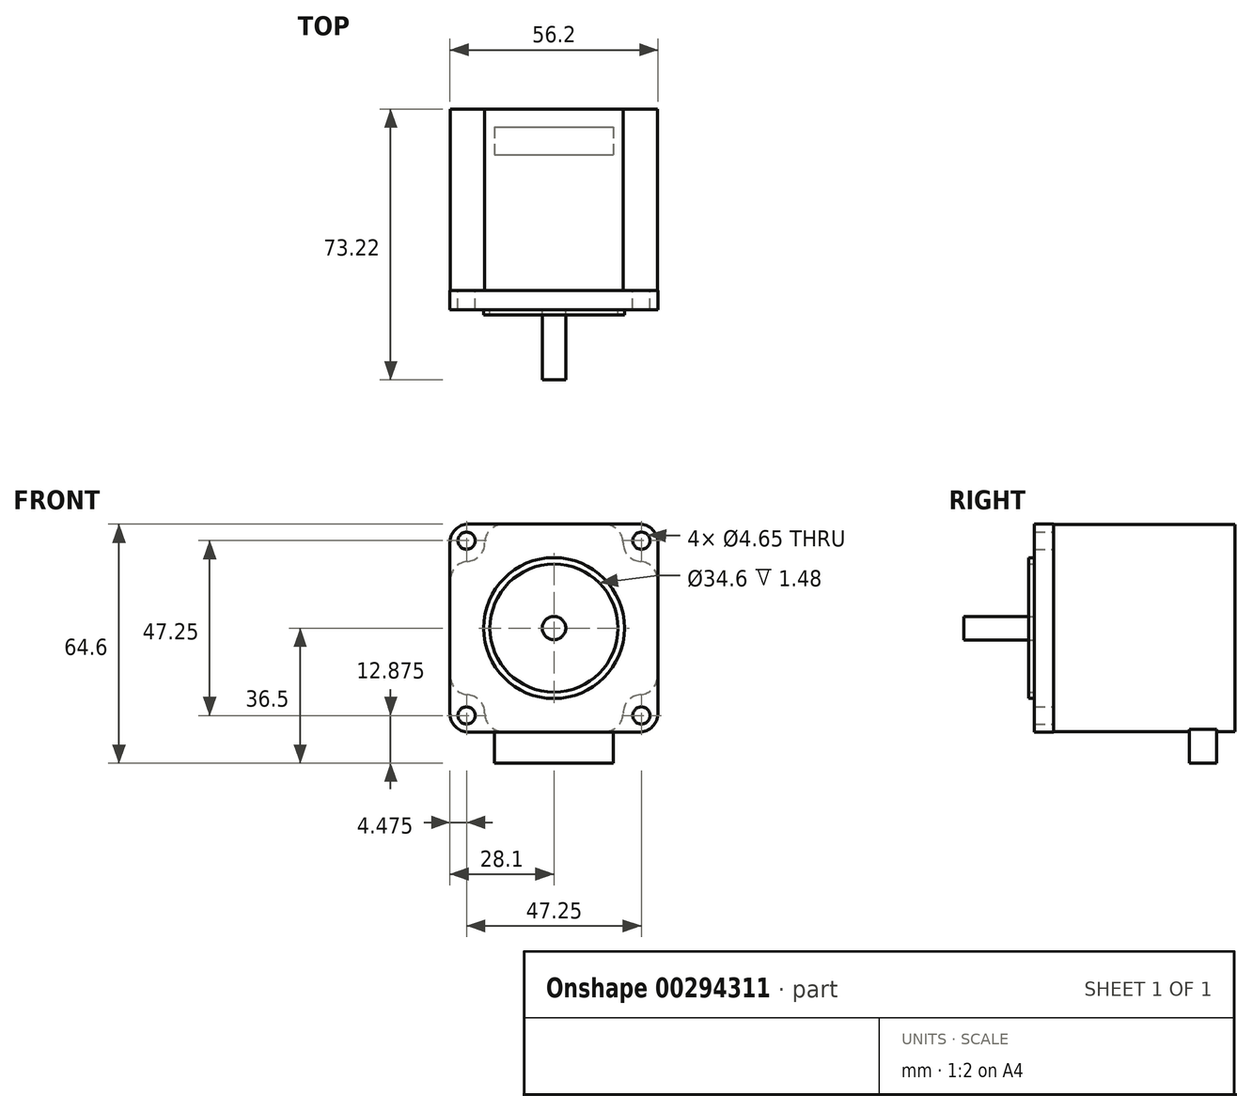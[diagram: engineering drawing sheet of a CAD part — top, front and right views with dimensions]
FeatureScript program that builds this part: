
annotation { "Feature Type Name" : "Feature", "Feature Type Description" : "" }
export const myFeature = defineFeature(function(context is Context, id is Id, definition is map)
    precondition{}
    {
        {
            var Q0;
            Q0=qCreatedBy(makeId("Front.planeOp"),FACE);
            var sketch = newSketch(context, id + "F0", { "sketchPlane" : qUnion([Q0])});
            skLineSegment(sketch, "E0.bottom", {"start": v(23.1, 28.1) * mm, "end": v(-23.1, 28.1) * mm});
            skLineSegment(sketch, "E0.top", {"start": v(23.1, -28.1) * mm, "end": v(-23.1, -28.1) * mm});
            skLineSegment(sketch, "E0.left", {"start": v(28.1, 23.1) * mm, "end": v(28.1, -23.1) * mm});
            skLineSegment(sketch, "E0.right", {"start": v(-28.1, 23.1) * mm, "end": v(-28.1, -23.1) * mm});
            skPoint(sketch, "E0.middle", {"position": v(0, 0) * mm});
            skLineSegment(sketch, "E1.bottom", {"start": v(23.62, 23.62) * mm, "end": v(-23.62, 23.62) * mm, "construction": true});
            skLineSegment(sketch, "E1.top", {"start": v(23.62, -23.62) * mm, "end": v(-23.62, -23.62) * mm, "construction": true});
            skLineSegment(sketch, "E1.left", {"start": v(23.62, 23.62) * mm, "end": v(23.62, -23.62) * mm, "construction": true});
            skLineSegment(sketch, "E1.right", {"start": v(-23.62, 23.62) * mm, "end": v(-23.62, -23.62) * mm, "construction": true});
            skCircle(sketch, "E2", {"center": v(23.62, 23.62) * mm, "radius": 2.33 * mm});
            skLineSegment(sketch, "E3.direction1", {"start": v(23.62, 23.62) * mm, "end": v(-1.38, 23.62) * mm, "construction": true});
            skCircle(sketch, "E4.MirrorC", {"center": v(-23.62, 23.62) * mm, "radius": 2.33 * mm});
            skCircle(sketch, "E5.MirrorC", {"center": v(23.62, -23.62) * mm, "radius": 2.33 * mm});
            skCircle(sketch, "E6.MirrorC", {"center": v(-23.62, -23.62) * mm, "radius": 2.33 * mm});
            skPoint(sketch, "E7.visualSharp", {"position": v(-28.1, 28.1) * mm});
            skArc(sketch, "E7.filletArc", {"start": v(-23.1, 28.1) * mm, "mid": v(-26.64, 26.64) * mm, "end": v(-28.1, 23.1) * mm});
            skPoint(sketch, "E8.visualSharp", {"position": v(28.1, 28.1) * mm});
            skArc(sketch, "E8.filletArc", {"start": v(28.1, 23.1) * mm, "mid": v(26.64, 26.64) * mm, "end": v(23.1, 28.1) * mm});
            skPoint(sketch, "E9.visualSharp", {"position": v(28.1, -28.1) * mm});
            skArc(sketch, "E9.filletArc", {"start": v(23.1, -28.1) * mm, "mid": v(26.64, -26.64) * mm, "end": v(28.1, -23.1) * mm});
            skPoint(sketch, "E10.visualSharp", {"position": v(-28.1, -28.1) * mm});
            skArc(sketch, "E10.filletArc", {"start": v(-28.1, -23.1) * mm, "mid": v(-26.64, -26.64) * mm, "end": v(-23.1, -28.1) * mm});
            skSolve(sketch);
        }
        {
            var Q0;
            Q0 = qSketchRegion(id + "F0", true);
            extrude(context, id + "F1", {"entities" : qUnion([Q0]), "depth" : 5.2 * mm, "offsetDistance" : 25 * mm});
        }
        {
            var Q0;
            Q0=makeQuery(id+"F1.opExtrude","CAP_FACE",FACE,{"disambiguationData":[OSD([sQuery(id+"F0.wireOp",EDGE,"E0.bottom"),sQuery(id+"F0.wireOp",EDGE,"E0.top"),sQuery(id+"F0.wireOp",EDGE,"E0.left"),sQuery(id+"F0.wireOp",EDGE,"E0.right"),sQuery(id+"F0.wireOp",EDGE,"E2"),sQuery(id+"F0.wireOp",EDGE,"E4.MirrorC"),sQuery(id+"F0.wireOp",EDGE,"E5.MirrorC"),sQuery(id+"F0.wireOp",EDGE,"E6.MirrorC"),sQuery(id+"F0.wireOp",EDGE,"E7.filletArc"),sQuery(id+"F0.wireOp",EDGE,"E8.filletArc"),sQuery(id+"F0.wireOp",EDGE,"E9.filletArc"),sQuery(id+"F0.wireOp",EDGE,"E10.filletArc")])],"isStart":false});
            var sketch = newSketch(context, id + "F2", { "sketchPlane" : qUnion([Q0])});
            skCircle(sketch, "E11", {"center": v(0, 0) * mm, "radius": 19.04 * mm});
            skCircle(sketch, "E12", {"center": v(0, 0) * mm, "radius": 17.3 * mm});
            skSolve(sketch);
        }
        {
            var Q0;
            Q0 = qSketchRegion(id + "F2", true);
            extrude(context, id + "F3", {"entities" : qUnion([Q0]), "operationType" : NewBodyOperationType.ADD, "depth" : 1.48 * mm, "offsetDistance" : 25 * mm});
        }
        {
            var Q0;
            Q0=makeQuery(id+"F3.boolean.opBoolean","SPLIT",FACE,{"disambiguationData":[TD([makeQuery(id+"F3.opExtrude","SWEPT_FACE",FACE,{"disambiguationData":[OSD([sQuery(id+"F2.wireOp",EDGE,"E12")])]})])],"derivedFrom":makeQuery(id+"F1.opExtrude","CAP_FACE",FACE,{"disambiguationData":[OSD([sQuery(id+"F0.wireOp",EDGE,"E0.bottom"),sQuery(id+"F0.wireOp",EDGE,"E0.top"),sQuery(id+"F0.wireOp",EDGE,"E0.left"),sQuery(id+"F0.wireOp",EDGE,"E0.right"),sQuery(id+"F0.wireOp",EDGE,"E2"),sQuery(id+"F0.wireOp",EDGE,"E4.MirrorC"),sQuery(id+"F0.wireOp",EDGE,"E5.MirrorC"),sQuery(id+"F0.wireOp",EDGE,"E6.MirrorC"),sQuery(id+"F0.wireOp",EDGE,"E7.filletArc"),sQuery(id+"F0.wireOp",EDGE,"E8.filletArc"),sQuery(id+"F0.wireOp",EDGE,"E9.filletArc"),sQuery(id+"F0.wireOp",EDGE,"E10.filletArc")])],"isStart":false})});
            var sketch = newSketch(context, id + "F4", { "sketchPlane" : qUnion([Q0])});
            skCircle(sketch, "E13", {"center": v(0, 0) * mm, "radius": 3.17 * mm});
            skSolve(sketch);
        }
        {
            var Q0;
            Q0=makeQuery(id+"F1.opExtrude","CAP_FACE",FACE,{"disambiguationData":[OSD([sQuery(id+"F0.wireOp",EDGE,"E0.bottom"),sQuery(id+"F0.wireOp",EDGE,"E0.top"),sQuery(id+"F0.wireOp",EDGE,"E0.left"),sQuery(id+"F0.wireOp",EDGE,"E0.right"),sQuery(id+"F0.wireOp",EDGE,"E2"),sQuery(id+"F0.wireOp",EDGE,"E4.MirrorC"),sQuery(id+"F0.wireOp",EDGE,"E5.MirrorC"),sQuery(id+"F0.wireOp",EDGE,"E6.MirrorC"),sQuery(id+"F0.wireOp",EDGE,"E7.filletArc"),sQuery(id+"F0.wireOp",EDGE,"E8.filletArc"),sQuery(id+"F0.wireOp",EDGE,"E9.filletArc"),sQuery(id+"F0.wireOp",EDGE,"E10.filletArc")])],"isStart":true});
            var sketch = newSketch(context, id + "F5", { "sketchPlane" : qUnion([Q0])});
            skLineSegment(sketch, "E14.bottom", {"start": v(-13.7, 28) * mm, "end": v(13.7, 28) * mm});
            skLineSegment(sketch, "E14.top", {"start": v(-13.7, -28) * mm, "end": v(13.7, -28) * mm});
            skLineSegment(sketch, "E14.left", {"start": v(-28, 13.02) * mm, "end": v(-28, -13.02) * mm});
            skLineSegment(sketch, "E14.right", {"start": v(28, 13.02) * mm, "end": v(28, -13.02) * mm});
            skPoint(sketch, "E14.middle", {"position": v(0, 0) * mm});
            skLineSegment(sketch, "E15", {"start": v(-26.1, 0) * mm, "end": v(40.73, 0) * mm, "construction": true});
            skLineSegment(sketch, "E16", {"start": v(0, 26.91) * mm, "end": v(0, -26.91) * mm, "construction": true});
            skPoint(sketch, "E16.endSnap0", {"position": v(0, -28) * mm});
            skLineSegment(sketch, "E17.0", {"start": v(18.7, 23) * mm, "end": v(18.7, 23) * mm});
            skLineSegment(sketch, "E18.trimOffspring", {"start": v(23.35, 18.01) * mm, "end": v(23.35, 18.01) * mm});
            skPoint(sketch, "E19.orphan", {"position": v(28, 28) * mm});
            skPoint(sketch, "E20.visualSharp", {"position": v(18.7, 28) * mm});
            skArc(sketch, "E20.filletArc", {"start": v(18.7, 23) * mm, "mid": v(17.24, 26.54) * mm, "end": v(13.7, 28) * mm});
            skPoint(sketch, "E21.visualSharp", {"position": v(28, 17.69) * mm});
            skArc(sketch, "E21.filletArc", {"start": v(28, 13.02) * mm, "mid": v(26.66, 16.43) * mm, "end": v(23.35, 18.01) * mm});
            skPoint(sketch, "E22.visualSharp", {"position": v(18.7, 18.34) * mm});
            skArc(sketch, "E22.filletArc", {"start": v(18.7, 23) * mm, "mid": v(20.04, 19.6) * mm, "end": v(23.35, 18.01) * mm});
            skArc(sketch, "E23.MirrorCS", {"start": v(-18.7, 23) * mm, "mid": v(-17.24, 26.54) * mm, "end": v(-13.7, 28) * mm});
            skArc(sketch, "E24.MirrorCS", {"start": v(-18.7, 23) * mm, "mid": v(-20.04, 19.6) * mm, "end": v(-23.35, 18.01) * mm});
            skArc(sketch, "E25.MirrorCS", {"start": v(-28, 13.02) * mm, "mid": v(-26.66, 16.43) * mm, "end": v(-23.35, 18.01) * mm});
            skArc(sketch, "E26.MirrorCS", {"start": v(-28, -13.02) * mm, "mid": v(-26.66, -16.43) * mm, "end": v(-23.35, -18.01) * mm});
            skArc(sketch, "E27.MirrorCS", {"start": v(-18.7, -23) * mm, "mid": v(-20.04, -19.6) * mm, "end": v(-23.35, -18.01) * mm});
            skArc(sketch, "E28.MirrorCS", {"start": v(-18.7, -23) * mm, "mid": v(-17.24, -26.54) * mm, "end": v(-13.7, -28) * mm});
            skArc(sketch, "E29.MirrorCS", {"start": v(18.7, -23) * mm, "mid": v(17.24, -26.54) * mm, "end": v(13.7, -28) * mm});
            skArc(sketch, "E30.MirrorCS", {"start": v(18.7, -23) * mm, "mid": v(20.04, -19.6) * mm, "end": v(23.35, -18.01) * mm});
            skArc(sketch, "E31.MirrorCS", {"start": v(28, -13.02) * mm, "mid": v(26.66, -16.43) * mm, "end": v(23.35, -18.01) * mm});
            skPoint(sketch, "E32.orphan", {"position": v(-28, -28) * mm});
            skPoint(sketch, "E33.orphan", {"position": v(28, -28) * mm});
            skPoint(sketch, "E34.orphan", {"position": v(-28, 28) * mm});
            skSolve(sketch);
        }
        {
            var Q0;
            Q0 = qSketchRegion(id + "F5", true);
            extrude(context, id + "F6", {"entities" : qUnion([Q0]), "operationType" : NewBodyOperationType.ADD, "depth" : 49.02 * mm});
        }
        {
            var Q0;
            Q0 = qSketchRegion(id + "F4", true);
            extrude(context, id + "F7", {"entities" : qUnion([Q0]), "operationType" : NewBodyOperationType.ADD, "depth" : 19 * mm});
        }
        {
            var Q0;
            Q0=makeQuery(id+"F6.opExtrude","SWEPT_FACE",FACE,{"disambiguationData":[OSD([sQuery(id+"F5.wireOp",EDGE,"E14.top")])]});
            var sketch = newSketch(context, id + "F8", { "sketchPlane" : qUnion([Q0])});
            skLineSegment(sketch, "E35.bottom", {"start": v(-16.09, -36.68) * mm, "end": v(16.09, -36.68) * mm});
            skLineSegment(sketch, "E35.top", {"start": v(-16.09, -44.13) * mm, "end": v(16.1, -44.13) * mm});
            skLineSegment(sketch, "E35.left", {"start": v(-16.09, -36.68) * mm, "end": v(-16.09, -44.13) * mm});
            skLineSegment(sketch, "E35.right", {"start": v(16.1, -36.68) * mm, "end": v(16.1, -44.13) * mm});
            skPoint(sketch, "E35.middle", {"position": v(0, -40.4) * mm});
            skSolve(sketch);
        }
        {
            var Q0;
            Q0 = qSketchRegion(id + "F8", true);
            extrude(context, id + "F9", {"entities" : qUnion([Q0]), "operationType" : NewBodyOperationType.ADD, "endBound" : BoundingType.SYMMETRIC, "depth" : 17 * mm, "offsetDistance" : 25 * mm});
        }
    });
